# Revit family: DefaultType
name_source: partatom
category: Specialty Equipment
revit_build: Autodesk Revit 2018 (Build: 20180423_1000(x64)
units: mm (PartAtom-declared; Revit-internal decimal feet)

## family parameters
Always vertical = Yes
Cut with Voids When Loaded = No
OmniClass Number = 23.40.40.14.24
OmniClass Title = Food Dispensing Equipment
Part Type = Normal
Room Calculation Point = No
Round Connector Dimension = Use Diameter
Shared = No
Work Plane-Based = No

## types (1)
- DefaultType
    Assembly Code = E1090320
    CSI MasterFormat = 11 46 00
    Cold Water Connection Height = 1' - 5 1/2"
    Cold Water Flow = 0.264 GPM
    Cold Water Maximum Pressure = 124.00 psi
    Cold Water Minimum Pressure = 29.00 psi
    Cold Water RI Height = 0' - 0"
    Cold Water Size = 1"
    Cold Water Temperature Recommended = 40 °F
    Depth = 0' - 4 11/16"
    Description = Water Filter
    Foodservice Equipment Identifier = Yes
    Height = 1' - 6 1/4"
    Identify Quantity as Lot = Yes
    KCL SpecSheet URL = http://kclweb.kclcad.com
    KCLRef = KCL2C9,,44d91e82-04aa-478f-a02c-4dd25de865a0,VI,PURITY C300 QUELL ST,637475599520000000,6aab247b-bef6-4b92-84de-7421b6d27a09,ab611030-743f-4f48-897c-af1a01b9a17b
    Manufacturer = Vivreau
    Masterspec = Division 11
    Model = PURITY C300 Quell ST
    Plumbing Connection Type = NPT
    Specification by Manufacturer = Purity C Quell ST 300 water filtration kit, includes filter head, mount and filter cartridge. Capacity of 1057 gallons for coffee, espresso, vending.   Max operating pressure 125 psi, water intake temp 39-86 degrees Fahrenheit, Nominal flow (pressure loss at nominal flow) 60 I/h 3.6 PSI.   Dimensions w/d/h with filter head 4.9/4.6/18.3in , weight dry/wet 6.1/9.2lbs connection G3/8”, position horizontal and vertical.  Technology, decarbonization.  Systematic filter system, pre-filter, carbonate hardness reduction, activated carbon filtration and fine filtration.
    URL = www.vivreauwater.com/professional-filters
    URL Cutsheet = www.vivreauwater.com/purity_c_quell_st_spec-sheet
    Weight in Pounds = 6.17
    Width = 0' - 4 11/16"

## geometry (parser evidence)
native form markers: Sweep x10
no freeform markers — native parametric forms only
